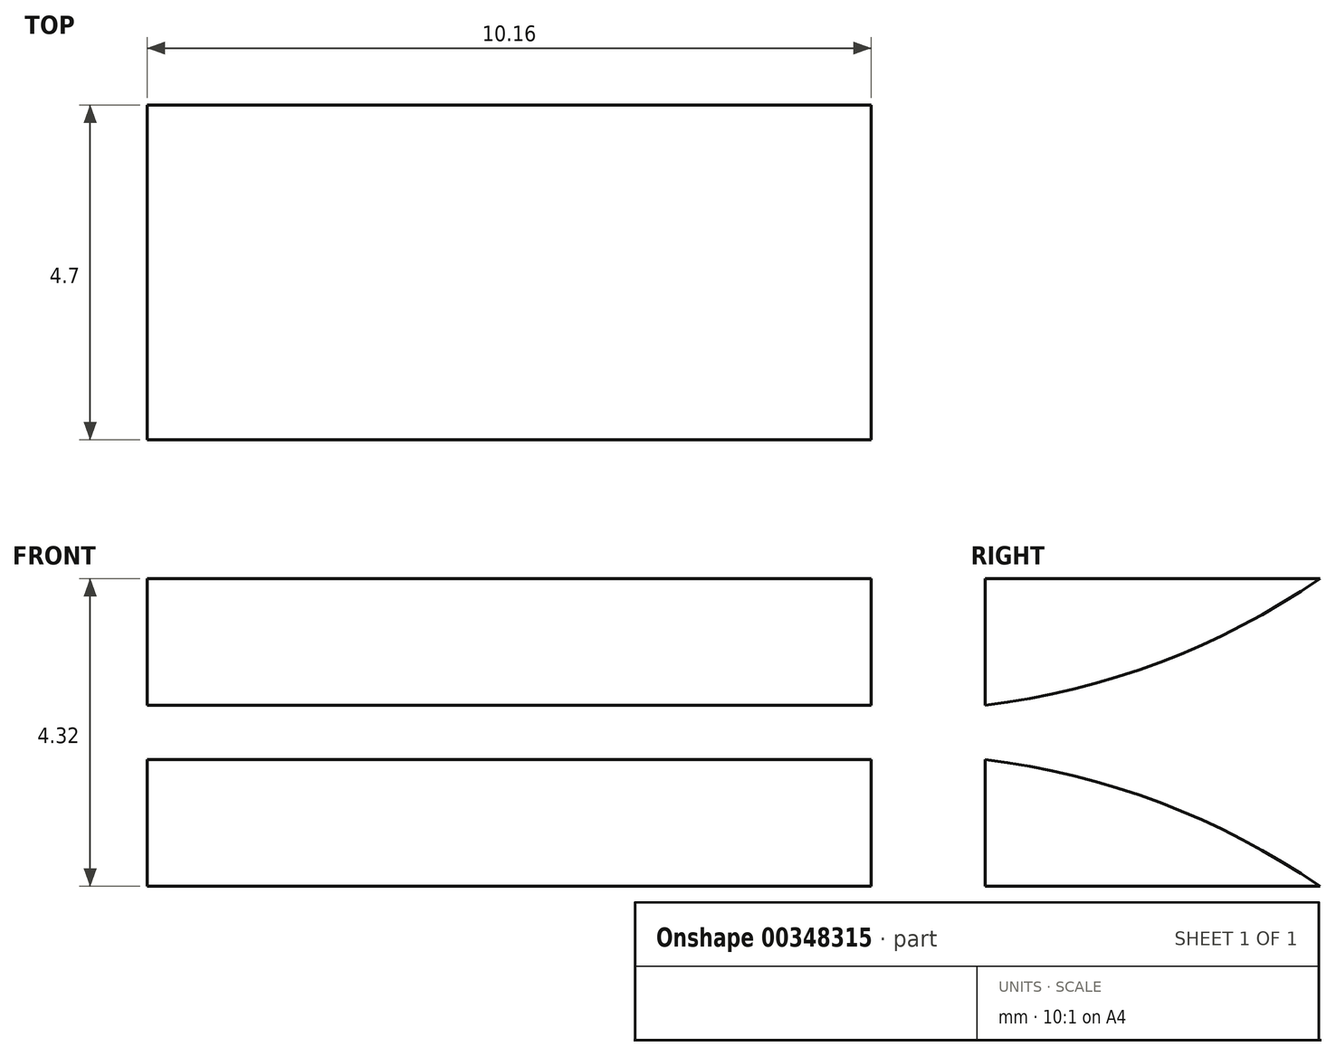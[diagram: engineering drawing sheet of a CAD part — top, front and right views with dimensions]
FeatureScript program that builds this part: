
annotation { "Feature Type Name" : "Feature", "Feature Type Description" : "" }
export const myFeature = defineFeature(function(context is Context, id is Id, definition is map)
    precondition{}
    {
        {
            var Q0;
            Q0=qCreatedBy(makeId("Front.planeOp"),FACE);
            var sketch = newSketch(context, id + "F0", { "sketchPlane" : qUnion([Q0])});
            skLineSegment(sketch, "E0.bottom", {"start": v(3.18, -2.16) * mm, "end": v(-3.18, -2.16) * mm});
            skLineSegment(sketch, "E0.top", {"start": v(3.18, 2.16) * mm, "end": v(-3.18, 2.16) * mm});
            skLineSegment(sketch, "E0.left", {"start": v(3.18, -2.16) * mm, "end": v(3.18, 2.16) * mm});
            skLineSegment(sketch, "E0.right", {"start": v(-3.18, -2.16) * mm, "end": v(-3.18, 2.16) * mm});
            skPoint(sketch, "E0.middle", {"position": v(0, 0) * mm});
            skSolve(sketch);
        }
        {
            var Q0;
            Q0=qSketchRegion(id+"F0",true);
            extrude(context, id + "F1", {"entities" : qUnion([Q0]), "oppositeDirection" : true, "depth" : 10.67 * mm});
        }
        {
            var Q0;
            Q0=qCreatedBy(makeId("Right.planeOp"),FACE);
            var sketch = newSketch(context, id + "F2", { "sketchPlane" : qUnion([Q0])});
            skCircle(sketch, "E1", {"center": v(2.41, 0.25) * mm, "radius": 1.14 * mm});
            skPoint(sketch, "E2.endSnap0", {"position": v(2.61, 0.97) * mm});
            skLineSegment(sketch, "E3", {"start": v(2.41, 0.25) * mm, "end": v(2.41, 5.84) * mm, "construction": true});
            skLineSegment(sketch, "E4.bottom", {"start": v(2.41, 2.2) * mm, "end": v(3.24, 2.2) * mm});
            skLineSegment(sketch, "E4.top", {"start": v(2.41, 0.72) * mm, "end": v(3.24, 0.72) * mm});
            skLineSegment(sketch, "E4.left", {"start": v(2.41, 2.2) * mm, "end": v(2.41, 0.72) * mm});
            skLineSegment(sketch, "E4.right", {"start": v(3.24, 2.2) * mm, "end": v(3.24, 0.72) * mm});
            skLineSegment(sketch, "E5.MirrorCS", {"start": v(1.59, 2.2) * mm, "end": v(1.59, 0.72) * mm});
            skLineSegment(sketch, "E6.MirrorCS", {"start": v(2.41, 0.72) * mm, "end": v(1.59, 0.72) * mm});
            skLineSegment(sketch, "E7.MirrorCS", {"start": v(2.41, 2.2) * mm, "end": v(1.59, 2.2) * mm});
            skLineSegment(sketch, "E8", {"start": v(4.36, 5.1) * mm, "end": v(4.36, -4.68) * mm, "construction": true});
            skCircle(sketch, "E9.MirrorC", {"center": v(6.3, 0.25) * mm, "radius": 1.14 * mm});
            skLineSegment(sketch, "E10.MirrorCS", {"start": v(5.47, 2.2) * mm, "end": v(5.47, 0.72) * mm});
            skPoint(sketch, "E11.MirrorP", {"position": v(6.1, 0.97) * mm});
            skLineSegment(sketch, "E12.MirrorCS", {"start": v(7.12, 2.2) * mm, "end": v(7.12, 0.72) * mm});
            skLineSegment(sketch, "E13.MirrorCS", {"start": v(6.3, 0.72) * mm, "end": v(7.12, 0.72) * mm});
            skLineSegment(sketch, "E14.MirrorCS", {"start": v(6.3, 2.2) * mm, "end": v(7.12, 2.2) * mm});
            skLineSegment(sketch, "E15.MirrorCS", {"start": v(6.3, 2.2) * mm, "end": v(5.47, 2.2) * mm});
            skLineSegment(sketch, "E16.MirrorCS", {"start": v(6.3, 0.72) * mm, "end": v(5.47, 0.72) * mm});
            skLineSegment(sketch, "E17.MirrorCS", {"start": v(6.3, 2.2) * mm, "end": v(6.3, 0.72) * mm});
            skSolve(sketch);
        }
        {
            var Q0;
            Q0=qSketchRegion(id+"F2",true);
            extrude(context, id + "F3", {"entities" : qUnion([Q0]), "operationType" : NewBodyOperationType.REMOVE, "endBound" : BoundingType.SYMMETRIC, "oppositeDirection" : true, "depth" : 6.35 * mm});
        }
        {
            var Q0;
            Q0=makeQuery(id+"F1.opExtrude","CAP_FACE",FACE,{"disambiguationData":[OSD([sQuery(id+"F0.wireOp",EDGE,"E0.bottom"),sQuery(id+"F0.wireOp",EDGE,"E0.top"),sQuery(id+"F0.wireOp",EDGE,"E0.left"),sQuery(id+"F0.wireOp",EDGE,"E0.right")])],"isStart":false});
            var sketch = newSketch(context, id + "F4", { "sketchPlane" : qUnion([Q0])});
            skLineSegment(sketch, "E18.bottom", {"start": v(-3.18, 2.16) * mm, "end": v(3.18, 2.16) * mm});
            skLineSegment(sketch, "E18.top", {"start": v(-3.18, 1.14) * mm, "end": v(3.18, 1.14) * mm});
            skLineSegment(sketch, "E18.left", {"start": v(-3.18, 2.16) * mm, "end": v(-3.18, 1.14) * mm});
            skLineSegment(sketch, "E18.right", {"start": v(3.18, 2.16) * mm, "end": v(3.18, 1.14) * mm});
            skLineSegment(sketch, "E19.bottom", {"start": v(-4.34, 0) * mm, "end": v(4.15, 0) * mm, "construction": true});
            skLineSegment(sketch, "E19.top", {"start": v(-4.34, 0) * mm, "end": v(4.15, 0) * mm, "construction": true});
            skLineSegment(sketch, "E19.left", {"start": v(-4.34, 0) * mm, "end": v(-4.34, 0) * mm});
            skLineSegment(sketch, "E19.right", {"start": v(4.15, 0) * mm, "end": v(4.15, 0) * mm});
            skLineSegment(sketch, "E20.MirrorCS", {"start": v(-3.18, -1.14) * mm, "end": v(3.18, -1.14) * mm});
            skLineSegment(sketch, "E21.MirrorCS", {"start": v(3.18, -2.16) * mm, "end": v(3.18, -1.14) * mm});
            skLineSegment(sketch, "E22.MirrorCS", {"start": v(-3.18, -2.16) * mm, "end": v(3.18, -2.16) * mm});
            skLineSegment(sketch, "E23.MirrorCS", {"start": v(-3.18, -2.16) * mm, "end": v(-3.18, -1.14) * mm});
            skSolve(sketch);
        }
        {
            var Q0;
            Q0 = qSketchRegion(id + "F4", true);
            extrude(context, id + "F5", {"entities" : qUnion([Q0]), "operationType" : NewBodyOperationType.ADD, "oppositeDirection" : true, "depth" : -6.35 * mm});
        }
        {
            var Q0;
            Q0=makeQuery(id+"F5.opExtrude","CAP_FACE",FACE,{"disambiguationData":[OSD([sQuery(id+"F4.wireOp",EDGE,"E18.bottom"),sQuery(id+"F4.wireOp",EDGE,"E18.top"),sQuery(id+"F4.wireOp",EDGE,"E18.left"),sQuery(id+"F4.wireOp",EDGE,"E18.right")])],"isStart":false});
            var sketch = newSketch(context, id + "F6", { "sketchPlane" : qUnion([Q0])});
            skLineSegment(sketch, "E24.bottom", {"start": v(0, 4.76) * mm, "end": v(0, 4.76) * mm});
            skLineSegment(sketch, "E24.top", {"start": v(0, -4.93) * mm, "end": v(0, -4.93) * mm});
            skLineSegment(sketch, "E24.left", {"start": v(0, 4.76) * mm, "end": v(0, -4.93) * mm, "construction": true});
            skLineSegment(sketch, "E24.right", {"start": v(0, 4.76) * mm, "end": v(0, -4.93) * mm, "construction": true});
            skLineSegment(sketch, "E25.bottom", {"start": v(0, 2.16) * mm, "end": v(-5.08, 2.16) * mm});
            skLineSegment(sketch, "E25.top", {"start": v(0, 0.38) * mm, "end": v(-5.08, 0.38) * mm});
            skLineSegment(sketch, "E25.left", {"start": v(0, 2.16) * mm, "end": v(0, 0.38) * mm});
            skLineSegment(sketch, "E25.right", {"start": v(-5.08, 2.16) * mm, "end": v(-5.08, 0.38) * mm});
            skLineSegment(sketch, "E26.MirrorCS", {"start": v(0, 2.16) * mm, "end": v(5.08, 2.16) * mm});
            skLineSegment(sketch, "E27.MirrorCS", {"start": v(5.08, 2.16) * mm, "end": v(5.08, 0.38) * mm});
            skLineSegment(sketch, "E28.MirrorCS", {"start": v(0, 0.38) * mm, "end": v(5.08, 0.38) * mm});
            skSolve(sketch);
        }
        {
            var Q0;
            {var subQ3=sQuery(id+"F6.wireOp",EDGE,"E25.top");Q0=makeQuery(id+"F6.imprint","IMPRINT",FACE,{"disambiguationData":[TD([[makeQuery(id+"F6.imprint","IMPRINT",EDGE,{"derivedFrom":subQ3}),-1.0]])]});}
            var Q1;
            {var subQ1=makeQuery(id+"F5.opExtrude","CAP_EDGE",EDGE,{"disambiguationData":[OSD([sQuery(id+"F4.wireOp",EDGE,"E18.left")])],"isStart":false});Q1=makeQuery(id+"F6.imprint","IMPRINT",FACE,{"disambiguationData":[TD([[makeQuery(id+"F6.imprint","IMPRINT",EDGE,{"derivedFrom":subQ1}),-1.0]])]});}
            var Q2;
            {var subQ5=makeQuery(id+"F5.opExtrude","CAP_EDGE",EDGE,{"disambiguationData":[OSD([sQuery(id+"F4.wireOp",EDGE,"E18.right")])],"isStart":false});Q2=makeQuery(id+"F6.imprint","IMPRINT",FACE,{"disambiguationData":[TD([[makeQuery(id+"F6.imprint","IMPRINT",EDGE,{"derivedFrom":subQ5}),1.0]])]});}
            var Q3;
            {var subQ0=sQuery(id+"F6.wireOp",EDGE,"E27.MirrorCS");Q3=makeQuery(id+"F6.imprint","IMPRINT",FACE,{"disambiguationData":[TD([[makeQuery(id+"F6.imprint","IMPRINT",EDGE,{"derivedFrom":subQ0}),-1.0]])]});}
            extrude(context, id + "F7", {"entities" : qUnion([Q0, Q1, Q2, Q3]), "depth" : 4.7 * mm});
        }
        {
            var Q0;
            Q0=makeQuery(id+"F7.opExtrude","SWEPT_FACE",FACE,{"disambiguationData":[OSD([sQuery(id+"F6.wireOp",EDGE,"E27.MirrorCS")])]});
            var sketch = newSketch(context, id + "F8", { "sketchPlane" : qUnion([Q0])});
            skArc(sketch, "E29", {"start": v(-21.72, 2.16) * mm, "mid": v(-19.48, 0.99) * mm, "end": v(-17.02, 0.38) * mm});
            skSolve(sketch);
        }
        {
            var Q0;
            Q0=makeQuery(id+"F8.imprint","IMPRINT",FACE,{"disambiguationData":[TD([[makeQuery(id+"F8.imprint","IMPRINT",EDGE,{"derivedFrom":sQuery(id+"F8.wireOp",EDGE,"E29")}),1.0]])]});
            var Q1;
            Q1=makeQuery(id+"F7.opExtrude","SWEPT_FACE",FACE,{"disambiguationData":[OSD([sQuery(id+"F6.wireOp",EDGE,"E25.right")])]});
            extrude(context, id + "F9", {"entities" : qUnion([Q0]), "operationType" : NewBodyOperationType.INTERSECT, "endBound" : BoundingType.UP_TO_SURFACE, "oppositeDirection" : true, "endBoundEntityFace" : qUnion([Q1]), "depth" : -10.16 * mm});
        }
        {
            var Q0;
            Q0=makeQuery(id+"F7.opExtrude","SWEPT_BODY",BODY,{"disambiguationData":[OSD([sQuery(id+"F6.wireOp",EDGE,"E25.bottom"),sQuery(id+"F6.wireOp",EDGE,"E25.top"),sQuery(id+"F6.wireOp",EDGE,"E25.right"),sQuery(id+"F6.wireOp",EDGE,"E26.MirrorCS"),sQuery(id+"F6.wireOp",EDGE,"E27.MirrorCS"),sQuery(id+"F6.wireOp",EDGE,"E28.MirrorCS")])]});
            var Q1;
            Q1=qCreatedBy(makeId("Top.planeOp"),FACE);
            mirror(context, id + "F10", {"entities" : qUnion([Q0]), "mirrorPlane" : qUnion([Q1])});
        }
    });
